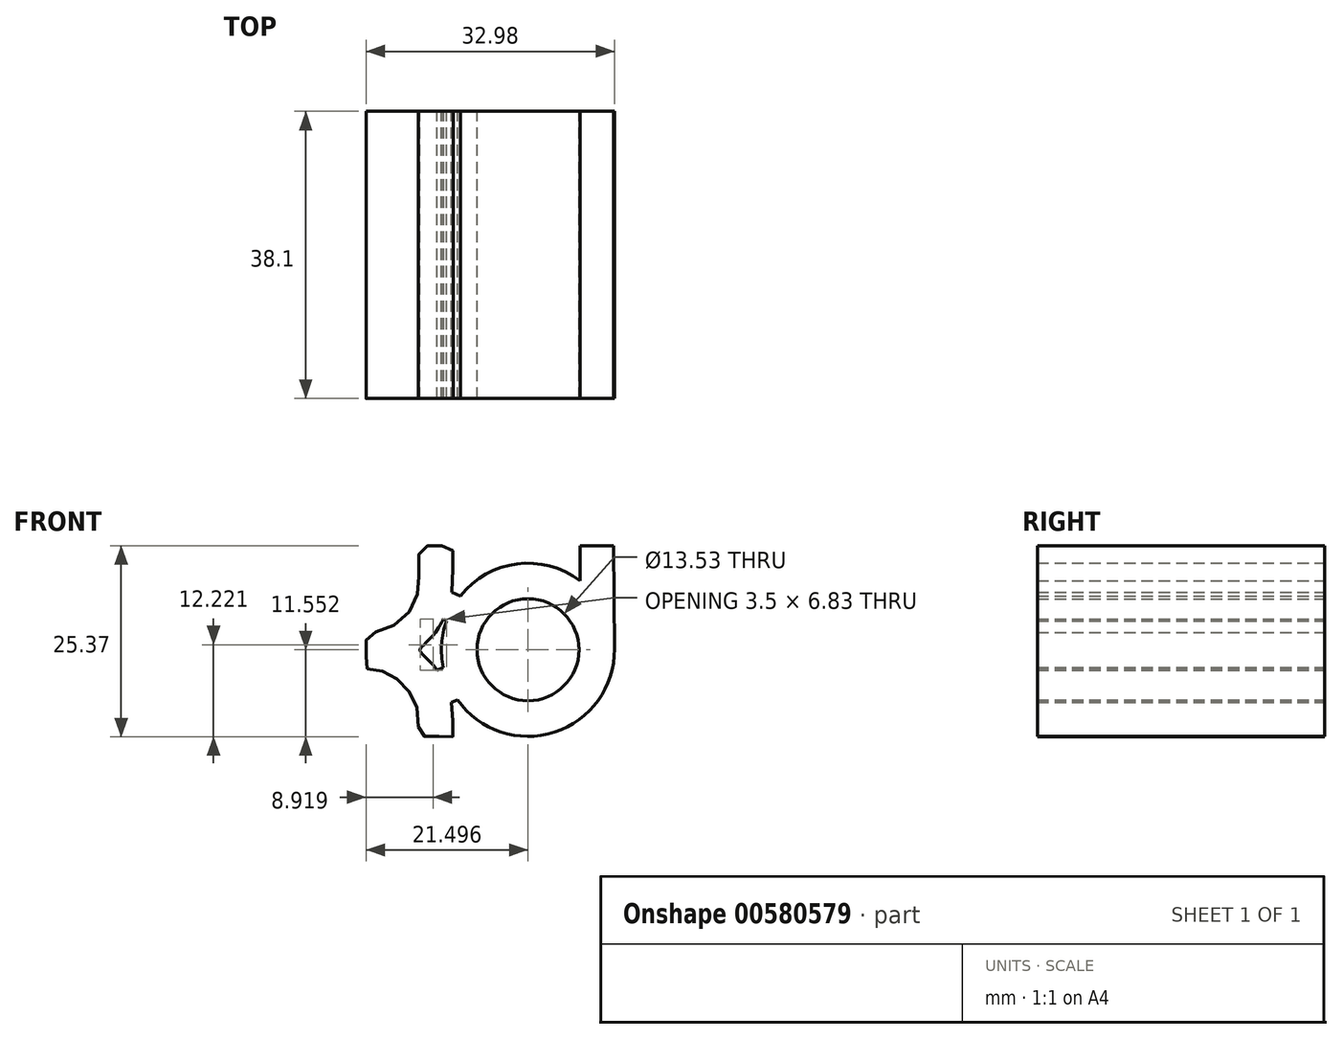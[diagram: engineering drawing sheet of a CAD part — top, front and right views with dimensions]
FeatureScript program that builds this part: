
annotation { "Feature Type Name" : "Feature", "Feature Type Description" : "" }
export const myFeature = defineFeature(function(context is Context, id is Id, definition is map)
    precondition{}
    {
        {
            var Q0;
            Q0=qCreatedBy(makeId("Front.planeOp"),FACE);
            var sketch = newSketch(context, id + "F0", { "sketchPlane" : qUnion([Q0])});
            skLineSegment(sketch, "E0", {"start": v(0, 0) * mm, "end": v(0, 38.1) * mm});
            skLineSegment(sketch, "E1", {"start": v(0, 38.1) * mm, "end": v(38.1, 38.1) * mm});
            skLineSegment(sketch, "E2", {"start": v(38.1, 38.1) * mm, "end": v(38.1, 0) * mm});
            skLineSegment(sketch, "E3", {"start": v(38.1, 0) * mm, "end": v(0, 0) * mm});
            skSolve(sketch);
        }
        {
            var Q0;
            Q0=makeQuery(id+"F0.imprint","IMPRINT",FACE,{"disambiguationData":[TD([[makeQuery(id+"F0.imprint","IMPRINT",EDGE,{"derivedFrom":sQuery(id+"F0.wireOp",EDGE,"E0")}),-1.0]])]});
            extrude(context, id + "F1", {"entities" : qUnion([Q0]), "depth" : 38.1 * mm, "offsetDistance" : 25.4 * mm});
        }
        {
            var Q0;
            Q0=qCreatedBy(makeId("Front.planeOp"),FACE);
            var sketch = newSketch(context, id + "F2", { "sketchPlane" : qUnion([Q0])});
            skCircle(sketch, "E4", {"center": v(23.2, 17.86) * mm, "radius": 6.76 * mm});
            skFitSpline(sketch, "E5", {"points": [v(8.7, 31.44) * mm, v(8.7, 30.37) * mm, v(8.73, 29.14) * mm, v(8.73, 27.53) * mm, v(8.7, 26.58) * mm, v(8.6, 25.64) * mm, v(8.35, 24.78) * mm, v(7.88, 23.58) * mm, v(7.18, 22.6) * mm, v(6.27, 21.72) * mm, v(5.35, 21.03) * mm, v(4.34, 20.52) * mm, v(3.27, 20.27) * mm, v(2.07, 20.14) * mm, v(1.82, 20.14) * mm, v(1.76, 19.26) * mm, v(1.72, 18.47) * mm, v(1.72, 17.65) * mm, v(1.72, 16.8) * mm, v(1.72, 16.14) * mm, v(1.72, 15.66) * mm, v(1.72, 15.4) * mm, v(2.48, 15.38) * mm, v(3.24, 15.28) * mm, v(3.8, 15.03) * mm, v(4.44, 14.8) * mm, v(5.2, 14.46) * mm, v(5.83, 13.99) * mm, v(6.6, 13.34) * mm, v(7.25, 12.54) * mm, v(7.73, 11.8) * mm, v(8.18, 10.99) * mm, v(8.48, 10.09) * mm, v(8.61, 9.19) * mm, v(8.65, 7.99) * mm, v(8.65, 6.76) * mm, v(8.65, 6.36) * mm, v(9.28, 6.36) * mm, v(10.08, 6.4) * mm, v(10.75, 6.32) * mm, v(11.28, 6.36) * mm, v(11.91, 6.36) * mm, v(12.44, 6.36) * mm, v(12.98, 6.36) * mm, v(13.28, 6.36) * mm, v(13.28, 7.22) * mm, v(13.24, 8.02) * mm, v(13.24, 8.99) * mm, v(13.18, 10.02) * mm, v(12.94, 11.09) * mm, v(12.64, 12.08) * mm, v(12.24, 13.05) * mm, v(11.81, 13.95) * mm, v(11.11, 15.11) * mm, v(10.38, 16.11) * mm, v(9.6, 16.85) * mm, v(9.12, 17.37) * mm, v(8.82, 17.86) * mm, v(9.34, 18.45) * mm, v(9.72, 18.88) * mm, v(10.41, 19.57) * mm, v(11.02, 20.3) * mm, v(11.5, 21.08) * mm, v(12.18, 22.28) * mm, v(12.7, 23.62) * mm, v(13, 24.61) * mm, v(13.13, 26.17) * mm, v(13.17, 27.76) * mm, v(13.22, 29.19) * mm, v(13.21, 30.15) * mm, v(13.21, 31.04) * mm, v(13.24, 31.54) * mm, v(12.26, 31.65) * mm, v(11.78, 31.65) * mm, v(11.17, 31.67) * mm, v(10.57, 31.65) * mm, v(9.85, 31.62) * mm, v(9.18, 31.6) * mm, v(8.7, 31.44) * mm]});
            skArc(sketch, "E6", {"start": v(30.11, 27.03) * mm, "mid": v(12.94, 12.7) * mm, "end": v(34.68, 17.95) * mm});
            skLineSegment(sketch, "E7", {"start": v(30.11, 27.03) * mm, "end": v(30.11, 31.68) * mm});
            skLineSegment(sketch, "E8", {"start": v(30.11, 31.68) * mm, "end": v(34.57, 31.68) * mm});
            skLineSegment(sketch, "E9", {"start": v(34.57, 31.68) * mm, "end": v(34.68, 17.95) * mm});
            skLineSegment(sketch, "E10", {"start": v(14.2, 25) * mm, "end": v(13.1, 25.5) * mm});
            skLineSegment(sketch, "E11", {"start": v(12, 21.95) * mm, "end": v(12.37, 21.68) * mm});
            skLineSegment(sketch, "E12", {"start": v(13, 10.86) * mm, "end": v(13.83, 11.21) * mm});
            skLineSegment(sketch, "E13", {"start": v(11.95, 15.53) * mm, "end": v(11.11, 15.11) * mm});
            skLineSegment(sketch, "E14.bottom", {"start": v(0, 0) * mm, "end": v(39.69, 0) * mm});
            skLineSegment(sketch, "E14.top", {"start": v(0, 39.3) * mm, "end": v(39.69, 39.3) * mm});
            skLineSegment(sketch, "E14.left", {"start": v(0, 0) * mm, "end": v(0, 39.3) * mm});
            skLineSegment(sketch, "E14.right", {"start": v(39.69, 0) * mm, "end": v(39.69, 39.3) * mm});
            skSolve(sketch);
        }
        {
            var Q0;
            {var subQ5=sQuery(id+"F2.wireOp",EDGE,"E7");Q0=makeQuery(id+"F2.imprint","IMPRINT",FACE,{"disambiguationData":[TD([[makeQuery(id+"F2.imprint","IMPRINT",EDGE,{"derivedFrom":subQ5}),1.0]])]});}
            var Q1;
            {var subQ0=sQuery(id+"F2.wireOp",EDGE,"E11");Q1=makeQuery(id+"F2.imprint","IMPRINT",FACE,{"disambiguationData":[TD([[makeQuery(id+"F2.imprint","IMPRINT",EDGE,{"derivedFrom":subQ0}),-1.0]])]});}
            var Q2;
            Q2=makeQuery(id+"F2.imprint","IMPRINT",FACE,{"disambiguationData":[TD([[makeQuery(id+"F2.imprint","IMPRINT",EDGE,{"derivedFrom":sQuery(id+"F2.wireOp",EDGE,"E4")}),1.0]])]});
            extrude(context, id + "F3", {"entities" : qUnion([Q0, Q1, Q2]), "operationType" : NewBodyOperationType.REMOVE, "depth" : 38.1 * mm, "offsetDistance" : 25.4 * mm});
        }
    });
